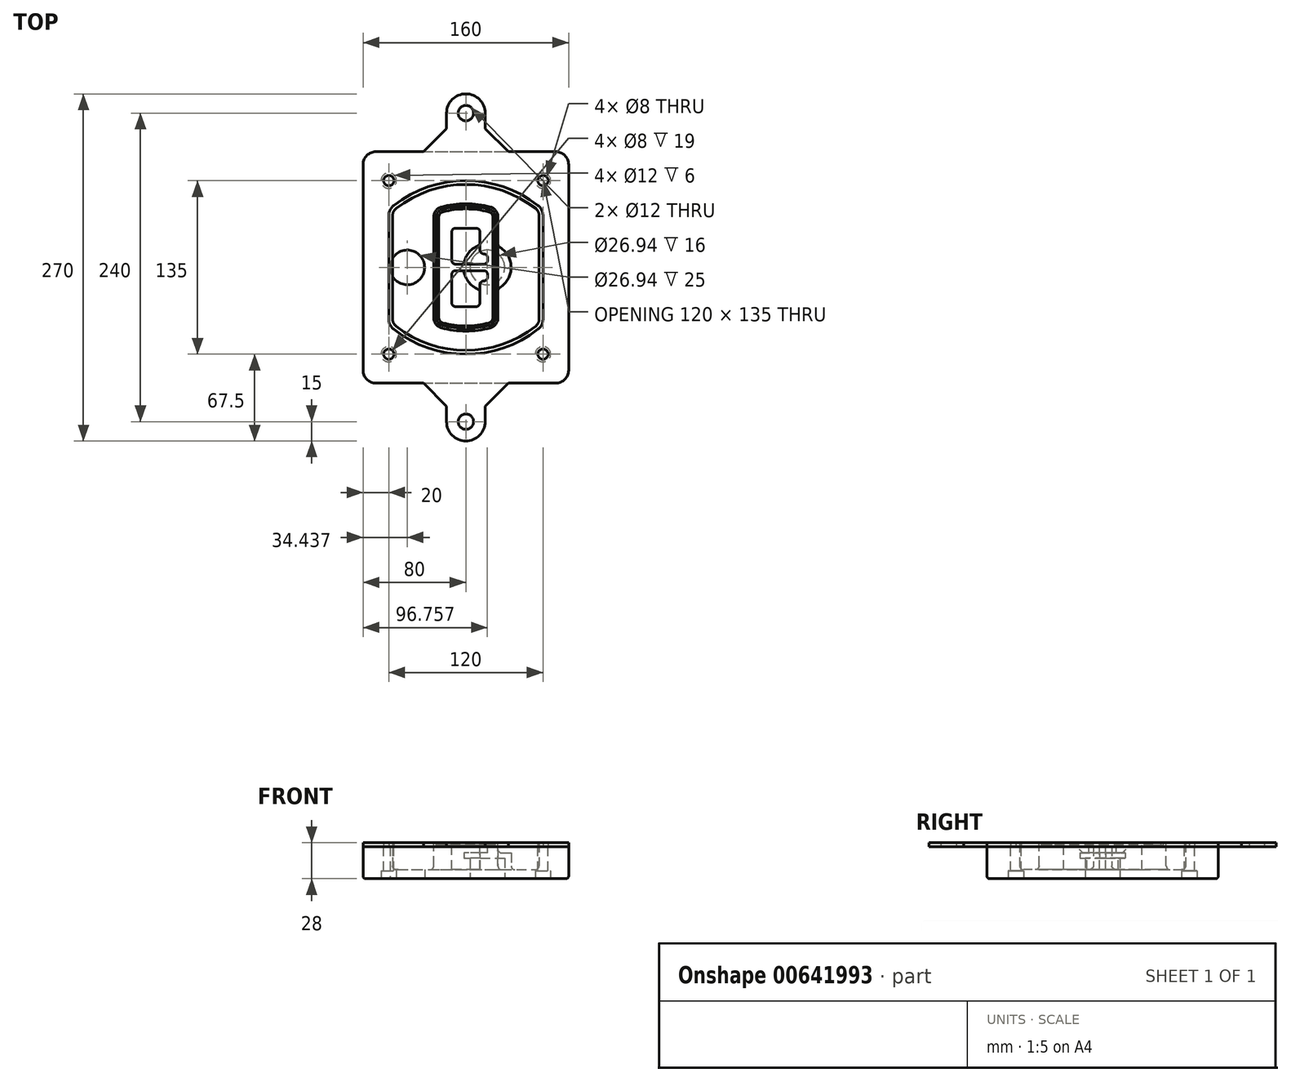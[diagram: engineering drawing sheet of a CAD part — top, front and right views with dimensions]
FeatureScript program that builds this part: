
annotation { "Feature Type Name" : "Feature", "Feature Type Description" : "" }
export const myFeature = defineFeature(function(context is Context, id is Id, definition is map)
    precondition{}
    {
        {
            var Q0;
            Q0=qCreatedBy(makeId("Top.planeOp"),FACE);
            var sketch = newSketch(context, id + "F0", { "sketchPlane" : qUnion([Q0])});
            skPoint(sketch, "E0.rect.middle", {"position": v(0, 0) * mm});
            skLineSegment(sketch, "E1.bottom", {"start": v(-70, -90) * mm, "end": v(70, -90) * mm});
            skLineSegment(sketch, "E1.top", {"start": v(-70, 90) * mm, "end": v(70, 90) * mm});
            skLineSegment(sketch, "E1.left", {"start": v(-80, -80) * mm, "end": v(-80, 80) * mm});
            skLineSegment(sketch, "E1.right", {"start": v(80, -80) * mm, "end": v(80, 80) * mm});
            skLineSegment(sketch, "E2", {"start": v(-80, 90) * mm, "end": v(80, -90) * mm, "construction": true});
            skLineSegment(sketch, "E3", {"start": v(80, 90) * mm, "end": v(-80, -90) * mm, "construction": true});
            skCircle(sketch, "E4", {"center": v(-60, 67.5) * mm, "radius": 4 * mm});
            skCircle(sketch, "E5", {"center": v(60, 67.5) * mm, "radius": 4 * mm});
            skCircle(sketch, "E6", {"center": v(60, -67.5) * mm, "radius": 4 * mm});
            skCircle(sketch, "E7", {"center": v(-60, -67.5) * mm, "radius": 4 * mm});
            skLineSegment(sketch, "E8", {"start": v(-60, 67.5) * mm, "end": v(60, 67.5) * mm, "construction": true});
            skLineSegment(sketch, "E9", {"start": v(60, 67.5) * mm, "end": v(60, -67.5) * mm, "construction": true});
            skLineSegment(sketch, "E10", {"start": v(60, -67.5) * mm, "end": v(-60, -67.5) * mm, "construction": true});
            skLineSegment(sketch, "E11", {"start": v(-60, -67.5) * mm, "end": v(-60, 67.5) * mm, "construction": true});
            skLineSegment(sketch, "E12", {"start": v(-60, 40.3) * mm, "end": v(-60, -40.3) * mm});
            skLineSegment(sketch, "E13", {"start": v(60, 40.3) * mm, "end": v(60, -40.3) * mm});
            skArc(sketch, "E14", {"start": v(56.15, 48.18) * mm, "mid": v(0, 67.5) * mm, "end": v(-56.15, 48.18) * mm});
            skArc(sketch, "E15", {"start": v(-56.15, -48.18) * mm, "mid": v(0, -67.5) * mm, "end": v(56.15, -48.18) * mm});
            skLineSegment(sketch, "E16", {"start": v(-60, 0) * mm, "end": v(60, 0) * mm, "construction": true});
            skPoint(sketch, "E17.visualSharp", {"position": v(-60, -45) * mm});
            skArc(sketch, "E17.filletArc", {"start": v(-60, -40.3) * mm, "mid": v(-58.99, -44.68) * mm, "end": v(-56.15, -48.18) * mm});
            skPoint(sketch, "E18.visualSharp", {"position": v(-60, 45) * mm});
            skArc(sketch, "E18.filletArc", {"start": v(-56.15, 48.18) * mm, "mid": v(-58.99, 44.68) * mm, "end": v(-60, 40.3) * mm});
            skPoint(sketch, "E19.visualSharp", {"position": v(60, 45) * mm});
            skArc(sketch, "E19.filletArc", {"start": v(60, 40.3) * mm, "mid": v(58.99, 44.68) * mm, "end": v(56.15, 48.18) * mm});
            skPoint(sketch, "E20.visualSharp", {"position": v(60, -45) * mm});
            skArc(sketch, "E20.filletArc", {"start": v(56.15, -48.18) * mm, "mid": v(58.99, -44.68) * mm, "end": v(60, -40.3) * mm});
            skPoint(sketch, "E21.visualSharp", {"position": v(-80, 90) * mm});
            skArc(sketch, "E21.filletArc", {"start": v(-70, 90) * mm, "mid": v(-77.07, 87.07) * mm, "end": v(-80, 80) * mm});
            skPoint(sketch, "E22.visualSharp", {"position": v(80, 90) * mm});
            skArc(sketch, "E22.filletArc", {"start": v(80, 80) * mm, "mid": v(77.07, 87.07) * mm, "end": v(70, 90) * mm});
            skPoint(sketch, "E23.visualSharp", {"position": v(80, -90) * mm});
            skArc(sketch, "E23.filletArc", {"start": v(70, -90) * mm, "mid": v(77.07, -87.07) * mm, "end": v(80, -80) * mm});
            skPoint(sketch, "E24.visualSharp", {"position": v(-80, -90) * mm});
            skArc(sketch, "E24.filletArc", {"start": v(-80, -80) * mm, "mid": v(-77.07, -87.07) * mm, "end": v(-70, -90) * mm});
            skArc(sketch, "E25.0", {"start": v(57, 40.3) * mm, "mid": v(56.3, 43.36) * mm, "end": v(54.3, 45.81) * mm});
            skLineSegment(sketch, "E25.1", {"start": v(57, 40.3) * mm, "end": v(57, -40.3) * mm});
            skArc(sketch, "E25.2", {"start": v(54.3, -45.81) * mm, "mid": v(56.3, -43.36) * mm, "end": v(57, -40.3) * mm});
            skArc(sketch, "E25.3", {"start": v(-54.3, -45.81) * mm, "mid": v(0, -64.5) * mm, "end": v(54.3, -45.81) * mm});
            skArc(sketch, "E25.4", {"start": v(-57, -40.3) * mm, "mid": v(-56.3, -43.36) * mm, "end": v(-54.3, -45.81) * mm});
            skArc(sketch, "E25.5", {"start": v(54.3, 45.81) * mm, "mid": v(0, 64.5) * mm, "end": v(-54.3, 45.81) * mm});
            skLineSegment(sketch, "E25.6", {"start": v(-57, 40.3) * mm, "end": v(-57, -40.3) * mm});
            skArc(sketch, "E25.7", {"start": v(-54.3, 45.81) * mm, "mid": v(-56.3, 43.36) * mm, "end": v(-57, 40.3) * mm});
            skArc(sketch, "E26.0", {"start": v(-58.62, 51.33) * mm, "mid": v(-62.58, 46.43) * mm, "end": v(-64, 40.3) * mm});
            skArc(sketch, "E26.1", {"start": v(58.62, 51.33) * mm, "mid": v(0, 71.5) * mm, "end": v(-58.62, 51.33) * mm});
            skArc(sketch, "E26.2", {"start": v(64, 40.3) * mm, "mid": v(62.58, 46.43) * mm, "end": v(58.62, 51.33) * mm});
            skLineSegment(sketch, "E26.3", {"start": v(64, 40.3) * mm, "end": v(64, -40.3) * mm});
            skArc(sketch, "E26.4", {"start": v(58.62, -51.33) * mm, "mid": v(62.58, -46.43) * mm, "end": v(64, -40.3) * mm});
            skLineSegment(sketch, "E26.5", {"start": v(-64, 40.3) * mm, "end": v(-64, -40.3) * mm});
            skArc(sketch, "E26.6", {"start": v(-58.62, -51.33) * mm, "mid": v(0, -71.5) * mm, "end": v(58.62, -51.33) * mm});
            skArc(sketch, "E26.7", {"start": v(-64, -40.3) * mm, "mid": v(-62.58, -46.43) * mm, "end": v(-58.62, -51.33) * mm});
            skSolve(sketch);
        }
        {
            var Q0;
            Q0=makeQuery(id+"F0.imprint","IMPRINT",FACE,{"disambiguationData":[TD([[makeQuery(id+"F0.imprint","IMPRINT",EDGE,{"derivedFrom":sQuery(id+"F0.wireOp",EDGE,"E1.bottom")}),1.0]])]});
            var Q1;
            Q1=makeQuery(id+"F0.imprint","IMPRINT",FACE,{"disambiguationData":[TD([[makeQuery(id+"F0.imprint","IMPRINT",EDGE,{"derivedFrom":sQuery(id+"F0.wireOp",EDGE,"E12")}),1.0]])]});
            var Q2;
            Q2=makeQuery(id+"F0.imprint","IMPRINT",FACE,{"disambiguationData":[TD([[makeQuery(id+"F0.imprint","IMPRINT",EDGE,{"derivedFrom":sQuery(id+"F0.wireOp",EDGE,"E25.0")}),1.0]])]});
            var Q3;
            Q3=makeQuery(id+"F0.imprint","IMPRINT",FACE,{"disambiguationData":[TD([[makeQuery(id+"F0.imprint","IMPRINT",EDGE,{"derivedFrom":sQuery(id+"F0.wireOp",EDGE,"E12")}),-1.0]])]});
            extrude(context, id + "F1", {"entities" : qUnion([Q0, Q1, Q2, Q3]), "oppositeDirection" : true, "depth" : 25 * mm});
        }
        {
            var Q0;
            Q0=makeQuery(id+"F0.imprint","IMPRINT",FACE,{"disambiguationData":[TD([[makeQuery(id+"F0.imprint","IMPRINT",EDGE,{"derivedFrom":sQuery(id+"F0.wireOp",EDGE,"E12")}),1.0]])]});
            extrude(context, id + "F2", {"entities" : qUnion([Q0]), "operationType" : NewBodyOperationType.ADD, "depth" : 3 * mm});
        }
        {
            var Q0;
            Q0=makeQuery(id+"F0.imprint","IMPRINT",FACE,{"disambiguationData":[TD([[makeQuery(id+"F0.imprint","IMPRINT",EDGE,{"derivedFrom":sQuery(id+"F0.wireOp",EDGE,"E25.0")}),1.0]])]});
            extrude(context, id + "F3", {"entities" : qUnion([Q0]), "operationType" : NewBodyOperationType.REMOVE, "oppositeDirection" : true, "depth" : 18 * mm});
        }
        {
            var Q0;
            Q0=makeQuery(id+"F2.opExtrude","CAP_FACE",FACE,{"disambiguationData":[OSD([sQuery(id+"F0.wireOp",EDGE,"E12"),sQuery(id+"F0.wireOp",EDGE,"E13"),sQuery(id+"F0.wireOp",EDGE,"E14"),sQuery(id+"F0.wireOp",EDGE,"E15"),sQuery(id+"F0.wireOp",EDGE,"E17.filletArc"),sQuery(id+"F0.wireOp",EDGE,"E18.filletArc"),sQuery(id+"F0.wireOp",EDGE,"E19.filletArc"),sQuery(id+"F0.wireOp",EDGE,"E20.filletArc"),sQuery(id+"F0.wireOp",EDGE,"E25.0"),sQuery(id+"F0.wireOp",EDGE,"E25.1"),sQuery(id+"F0.wireOp",EDGE,"E25.2"),sQuery(id+"F0.wireOp",EDGE,"E25.3"),sQuery(id+"F0.wireOp",EDGE,"E25.4"),sQuery(id+"F0.wireOp",EDGE,"E25.5"),sQuery(id+"F0.wireOp",EDGE,"E25.6"),sQuery(id+"F0.wireOp",EDGE,"E25.7")])],"isStart":false});
            var sketch = newSketch(context, id + "F4", { "sketchPlane" : qUnion([Q0])});
            skArc(sketch, "E27.0", {"start": v(-19.08, -46.97) * mm, "mid": v(0, -49.5) * mm, "end": v(19.08, -46.97) * mm});
            skArc(sketch, "E28.0", {"start": v(19.08, 46.97) * mm, "mid": v(0, 49.5) * mm, "end": v(-19.08, 46.97) * mm});
            skLineSegment(sketch, "E29", {"start": v(-25, 39.25) * mm, "end": v(-25, -39.25) * mm});
            skLineSegment(sketch, "E30", {"start": v(25, 39.25) * mm, "end": v(25, -39.25) * mm});
            skLineSegment(sketch, "E31", {"start": v(-25, 45.1) * mm, "end": v(25, 45.1) * mm, "construction": true});
            skLineSegment(sketch, "E32", {"start": v(-25, -45.1) * mm, "end": v(25, -45.1) * mm, "construction": true});
            skPoint(sketch, "E33.visualSharp", {"position": v(-25, 45.1) * mm});
            skArc(sketch, "E33.filletArc", {"start": v(-19.08, 46.97) * mm, "mid": v(-23.35, 44.11) * mm, "end": v(-25, 39.25) * mm});
            skPoint(sketch, "E34.visualSharp", {"position": v(25, 45.1) * mm});
            skArc(sketch, "E34.filletArc", {"start": v(25, 39.25) * mm, "mid": v(23.35, 44.11) * mm, "end": v(19.08, 46.97) * mm});
            skPoint(sketch, "E35.visualSharp", {"position": v(25, -45.1) * mm});
            skArc(sketch, "E35.filletArc", {"start": v(19.08, -46.97) * mm, "mid": v(23.35, -44.11) * mm, "end": v(25, -39.25) * mm});
            skPoint(sketch, "E36.visualSharp", {"position": v(-25, -45.1) * mm});
            skArc(sketch, "E36.filletArc", {"start": v(-25, -39.25) * mm, "mid": v(-23.35, -44.11) * mm, "end": v(-19.08, -46.97) * mm});
            skArc(sketch, "E37.0", {"start": v(54.3, 45.81) * mm, "mid": v(0, 64.5) * mm, "end": v(-54.3, 45.81) * mm});
            skArc(sketch, "E37.1", {"start": v(-54.3, 45.81) * mm, "mid": v(-56.3, 43.36) * mm, "end": v(-57, 40.3) * mm});
            skLineSegment(sketch, "E37.2", {"start": v(-57, 40.3) * mm, "end": v(-57, -40.3) * mm});
            skArc(sketch, "E37.3", {"start": v(-57, -40.3) * mm, "mid": v(-56.3, -43.36) * mm, "end": v(-54.3, -45.81) * mm});
            skArc(sketch, "E37.4", {"start": v(-54.3, -45.81) * mm, "mid": v(0, -64.5) * mm, "end": v(54.3, -45.81) * mm});
            skArc(sketch, "E37.5", {"start": v(54.3, -45.81) * mm, "mid": v(56.3, -43.36) * mm, "end": v(57, -40.3) * mm});
            skLineSegment(sketch, "E37.6", {"start": v(57, 40.3) * mm, "end": v(57, -40.3) * mm});
            skArc(sketch, "E37.7", {"start": v(57, 40.3) * mm, "mid": v(56.3, 43.36) * mm, "end": v(54.3, 45.81) * mm});
            skLineSegment(sketch, "E38.0", {"start": v(23, 39.25) * mm, "end": v(23, -39.25) * mm});
            skArc(sketch, "E38.1", {"start": v(18.56, -45.04) * mm, "mid": v(21.76, -42.9) * mm, "end": v(23, -39.25) * mm});
            skArc(sketch, "E38.2", {"start": v(-18.56, -45.04) * mm, "mid": v(0, -47.5) * mm, "end": v(18.56, -45.04) * mm});
            skArc(sketch, "E38.3", {"start": v(-23, -39.25) * mm, "mid": v(-21.76, -42.9) * mm, "end": v(-18.56, -45.04) * mm});
            skLineSegment(sketch, "E38.4", {"start": v(-23, 39.25) * mm, "end": v(-23, -39.25) * mm});
            skArc(sketch, "E38.5", {"start": v(23, 39.25) * mm, "mid": v(21.76, 42.9) * mm, "end": v(18.56, 45.04) * mm});
            skArc(sketch, "E38.6", {"start": v(-18.56, 45.04) * mm, "mid": v(-21.76, 42.9) * mm, "end": v(-23, 39.25) * mm});
            skArc(sketch, "E38.7", {"start": v(18.56, 45.04) * mm, "mid": v(0, 47.5) * mm, "end": v(-18.56, 45.04) * mm});
            skArc(sketch, "E39.0", {"start": v(21, 39.25) * mm, "mid": v(20.18, 41.68) * mm, "end": v(18.04, 43.1) * mm});
            skLineSegment(sketch, "E39.1", {"start": v(21, 39.25) * mm, "end": v(21, -39.25) * mm});
            skArc(sketch, "E39.2", {"start": v(18.04, -43.1) * mm, "mid": v(20.18, -41.68) * mm, "end": v(21, -39.25) * mm});
            skArc(sketch, "E39.3", {"start": v(-18.04, -43.1) * mm, "mid": v(0, -45.5) * mm, "end": v(18.04, -43.1) * mm});
            skArc(sketch, "E39.4", {"start": v(-21, -39.25) * mm, "mid": v(-20.18, -41.68) * mm, "end": v(-18.04, -43.1) * mm});
            skArc(sketch, "E39.5", {"start": v(18.04, 43.1) * mm, "mid": v(0, 45.5) * mm, "end": v(-18.04, 43.1) * mm});
            skLineSegment(sketch, "E39.6", {"start": v(-21, 39.25) * mm, "end": v(-21, -39.25) * mm});
            skArc(sketch, "E39.7", {"start": v(-18.04, 43.1) * mm, "mid": v(-20.18, 41.68) * mm, "end": v(-21, 39.25) * mm});
            skLineSegment(sketch, "E40", {"start": v(-25, 0) * mm, "end": v(25, 0) * mm, "construction": true});
            skLineSegment(sketch, "E41", {"start": v(-11, 5.5) * mm, "end": v(-11, 27.5) * mm});
            skLineSegment(sketch, "E42", {"start": v(-8, 30.5) * mm, "end": v(8, 30.5) * mm});
            skLineSegment(sketch, "E43", {"start": v(11, 27.5) * mm, "end": v(11, 13.5) * mm});
            skLineSegment(sketch, "E44", {"start": v(14, 10.5) * mm, "end": v(14, 10.5) * mm});
            skLineSegment(sketch, "E45", {"start": v(17, 7.5) * mm, "end": v(17, 5.5) * mm});
            skLineSegment(sketch, "E46", {"start": v(14, 2.5) * mm, "end": v(-8, 2.5) * mm});
            skPoint(sketch, "E47.visualSharp", {"position": v(-11, 30.5) * mm});
            skArc(sketch, "E47.filletArc", {"start": v(-8, 30.5) * mm, "mid": v(-10.12, 29.62) * mm, "end": v(-11, 27.5) * mm});
            skPoint(sketch, "E48.visualSharp", {"position": v(11, 30.5) * mm});
            skArc(sketch, "E48.filletArc", {"start": v(11, 27.5) * mm, "mid": v(10.12, 29.62) * mm, "end": v(8, 30.5) * mm});
            skPoint(sketch, "E49.visualSharp", {"position": v(11, 10.5) * mm});
            skArc(sketch, "E49.filletArc", {"start": v(11, 13.5) * mm, "mid": v(11.88, 11.38) * mm, "end": v(14, 10.5) * mm});
            skPoint(sketch, "E50.visualSharp", {"position": v(17, 10.5) * mm});
            skArc(sketch, "E50.filletArc", {"start": v(17, 7.5) * mm, "mid": v(16.12, 9.62) * mm, "end": v(14, 10.5) * mm});
            skPoint(sketch, "E51.visualSharp", {"position": v(17, 2.5) * mm});
            skArc(sketch, "E51.filletArc", {"start": v(14, 2.5) * mm, "mid": v(16.12, 3.38) * mm, "end": v(17, 5.5) * mm});
            skPoint(sketch, "E52.visualSharp", {"position": v(-11, 2.5) * mm});
            skArc(sketch, "E52.filletArc", {"start": v(-11, 5.5) * mm, "mid": v(-10.12, 3.38) * mm, "end": v(-8, 2.5) * mm});
            skLineSegment(sketch, "E53.0.MirrorCS", {"start": v(14, -2.5) * mm, "end": v(-8, -2.5) * mm});
            skArc(sketch, "E54.0.MirrorCS", {"start": v(-11, -5.5) * mm, "mid": v(-10.12, -3.38) * mm, "end": v(-8, -2.5) * mm});
            skLineSegment(sketch, "E55.0.MirrorCS", {"start": v(-11, -5.5) * mm, "end": v(-11, -27.5) * mm});
            skArc(sketch, "E56.0.MirrorCS", {"start": v(-8, -30.5) * mm, "mid": v(-10.12, -29.62) * mm, "end": v(-11, -27.5) * mm});
            skLineSegment(sketch, "E57.0.MirrorCS", {"start": v(-8, -30.5) * mm, "end": v(8, -30.5) * mm});
            skArc(sketch, "E58.0.MirrorCS", {"start": v(11, -27.5) * mm, "mid": v(10.12, -29.62) * mm, "end": v(8, -30.5) * mm});
            skLineSegment(sketch, "E59.0.MirrorCS", {"start": v(11, -27.5) * mm, "end": v(11, -13.5) * mm});
            skArc(sketch, "E60.0.MirrorCS", {"start": v(11, -13.5) * mm, "mid": v(11.88, -11.38) * mm, "end": v(14, -10.5) * mm});
            skArc(sketch, "E61.0.MirrorCS", {"start": v(17, -7.5) * mm, "mid": v(16.12, -9.62) * mm, "end": v(14, -10.5) * mm});
            skLineSegment(sketch, "E62.0.MirrorCS", {"start": v(17, -7.5) * mm, "end": v(17, -5.5) * mm});
            skArc(sketch, "E63.0.MirrorCS", {"start": v(14, -2.5) * mm, "mid": v(16.12, -3.38) * mm, "end": v(17, -5.5) * mm});
            skSolve(sketch);
        }
        {
            var Q0;
            Q0=makeQuery(id+"F4.imprint","IMPRINT",FACE,{"disambiguationData":[TD([[makeQuery(id+"F4.imprint","IMPRINT",EDGE,{"derivedFrom":sQuery(id+"F4.wireOp",EDGE,"E27.0")}),1.0]])]});
            var Q1;
            Q1=makeQuery(id+"F4.imprint","IMPRINT",FACE,{"disambiguationData":[TD([[makeQuery(id+"F4.imprint","IMPRINT",EDGE,{"derivedFrom":sQuery(id+"F4.wireOp",EDGE,"E38.0")}),-1.0]])]});
            var Q2;
            Q2=makeQuery(id+"F4.imprint","IMPRINT",FACE,{"disambiguationData":[TD([[makeQuery(id+"F4.imprint","IMPRINT",EDGE,{"derivedFrom":sQuery(id+"F4.wireOp",EDGE,"E39.0")}),1.0]])]});
            extrude(context, id + "F5", {"entities" : qUnion([Q0, Q1, Q2]), "operationType" : NewBodyOperationType.ADD, "endBound" : BoundingType.UP_TO_NEXT, "oppositeDirection" : true, "depth" : 25 * mm});
        }
        {
            var Q0;
            Q0=makeQuery(id+"F4.imprint","IMPRINT",FACE,{"disambiguationData":[TD([[makeQuery(id+"F4.imprint","IMPRINT",EDGE,{"derivedFrom":sQuery(id+"F4.wireOp",EDGE,"E38.0")}),-1.0]])]});
            extrude(context, id + "F6", {"entities" : qUnion([Q0]), "operationType" : NewBodyOperationType.REMOVE, "oppositeDirection" : true, "depth" : 2 * mm});
        }
        {
            var Q0;
            Q0=makeQuery(id+"F1.opExtrude","CAP_FACE",FACE,{"disambiguationData":[OSD([sQuery(id+"F0.wireOp",EDGE,"E1.bottom"),sQuery(id+"F0.wireOp",EDGE,"E1.top"),sQuery(id+"F0.wireOp",EDGE,"E1.left"),sQuery(id+"F0.wireOp",EDGE,"E1.right"),sQuery(id+"F0.wireOp",EDGE,"E4"),sQuery(id+"F0.wireOp",EDGE,"E5"),sQuery(id+"F0.wireOp",EDGE,"E6"),sQuery(id+"F0.wireOp",EDGE,"E7"),sQuery(id+"F0.wireOp",EDGE,"E21.filletArc"),sQuery(id+"F0.wireOp",EDGE,"E22.filletArc"),sQuery(id+"F0.wireOp",EDGE,"E23.filletArc"),sQuery(id+"F0.wireOp",EDGE,"E24.filletArc")])],"isStart":false});
            var sketch = newSketch(context, id + "F7", { "sketchPlane" : qUnion([Q0])});
            skCircle(sketch, "E64", {"center": v(16.76, 0) * mm, "radius": 13.47 * mm});
            skCircle(sketch, "E65", {"center": v(-45.56, 0) * mm, "radius": 13.47 * mm});
            skLineSegment(sketch, "E66", {"start": v(80, 0) * mm, "end": v(-80, 0) * mm});
            skCircle(sketch, "E67", {"center": v(16.76, 0) * mm, "radius": 18.47 * mm});
            skCircle(sketch, "E68", {"center": v(60, -67.5) * mm, "radius": 6 * mm});
            skCircle(sketch, "E69", {"center": v(-60, -67.5) * mm, "radius": 6 * mm});
            skCircle(sketch, "E70", {"center": v(-60, 67.5) * mm, "radius": 6 * mm});
            skCircle(sketch, "E71", {"center": v(60, 67.5) * mm, "radius": 6 * mm});
            skSolve(sketch);
        }
        {
            var Q0;
            {var subQ1=sQuery(id+"F7.wireOp",EDGE,"E66");var subQ4=sQuery(id+"F7.wireOp",EDGE,"E64");var subQ6=makeQuery(id+"F7.imprint","INTERSECT",VERTEX,{"disambiguationData":[OD(0.0)],"derivedFrom":[subQ4,subQ1]});Q0=makeQuery(id+"F7.imprint","IMPRINT",FACE,{"disambiguationData":[TD([[makeQuery(id+"F7.imprint","IMPRINT",EDGE,{"disambiguationData":[TD([[subQ6,-1.0]])],"derivedFrom":subQ4}),-1.0]])]});}
            var Q1;
            {var subQ0=sQuery(id+"F7.wireOp",EDGE,"E66");var subQ1=sQuery(id+"F7.wireOp",EDGE,"E64");var subQ3=makeQuery(id+"F7.imprint","INTERSECT",VERTEX,{"disambiguationData":[OD(0.0)],"derivedFrom":[subQ1,subQ0]});Q1=makeQuery(id+"F7.imprint","IMPRINT",FACE,{"disambiguationData":[TD([[makeQuery(id+"F7.imprint","IMPRINT",EDGE,{"disambiguationData":[TD([[subQ3,-1.0]])],"derivedFrom":subQ1}),1.0]])]});}
            var Q2;
            {var subQ0=sQuery(id+"F7.wireOp",EDGE,"E66");var subQ1=sQuery(id+"F7.wireOp",EDGE,"E64");var subQ3=makeQuery(id+"F7.imprint","INTERSECT",VERTEX,{"disambiguationData":[OD(0.0)],"derivedFrom":[subQ1,subQ0]});Q2=makeQuery(id+"F7.imprint","IMPRINT",FACE,{"disambiguationData":[TD([[makeQuery(id+"F7.imprint","IMPRINT",EDGE,{"disambiguationData":[TD([[subQ3,1.0]])],"derivedFrom":subQ1}),1.0]])]});}
            var Q3;
            {var subQ1=sQuery(id+"F7.wireOp",EDGE,"E66");var subQ4=sQuery(id+"F7.wireOp",EDGE,"E64");var subQ6=makeQuery(id+"F7.imprint","INTERSECT",VERTEX,{"disambiguationData":[OD(0.0)],"derivedFrom":[subQ4,subQ1]});Q3=makeQuery(id+"F7.imprint","IMPRINT",FACE,{"disambiguationData":[TD([[makeQuery(id+"F7.imprint","IMPRINT",EDGE,{"disambiguationData":[TD([[subQ6,1.0]])],"derivedFrom":subQ4}),-1.0]])]});}
            extrude(context, id + "F8", {"entities" : qUnion([Q0, Q1, Q2, Q3]), "operationType" : NewBodyOperationType.ADD, "oppositeDirection" : true, "depth" : 20 * mm});
        }
        {
            var Q0;
            {var subQ0=sQuery(id+"F7.wireOp",EDGE,"E66");var subQ1=sQuery(id+"F7.wireOp",EDGE,"E64");var subQ3=makeQuery(id+"F7.imprint","INTERSECT",VERTEX,{"disambiguationData":[OD(0.0)],"derivedFrom":[subQ1,subQ0]});Q0=makeQuery(id+"F7.imprint","IMPRINT",FACE,{"disambiguationData":[TD([[makeQuery(id+"F7.imprint","IMPRINT",EDGE,{"disambiguationData":[TD([[subQ3,-1.0]])],"derivedFrom":subQ1}),1.0]])]});}
            var Q1;
            {var subQ0=sQuery(id+"F7.wireOp",EDGE,"E66");var subQ1=sQuery(id+"F7.wireOp",EDGE,"E64");var subQ3=makeQuery(id+"F7.imprint","INTERSECT",VERTEX,{"disambiguationData":[OD(0.0)],"derivedFrom":[subQ1,subQ0]});Q1=makeQuery(id+"F7.imprint","IMPRINT",FACE,{"disambiguationData":[TD([[makeQuery(id+"F7.imprint","IMPRINT",EDGE,{"disambiguationData":[TD([[subQ3,1.0]])],"derivedFrom":subQ1}),1.0]])]});}
            extrude(context, id + "F9", {"entities" : qUnion([Q0, Q1]), "operationType" : NewBodyOperationType.REMOVE, "oppositeDirection" : true, "depth" : 16 * mm});
        }
        {
            var Q0;
            {var subQ0=sQuery(id+"F7.wireOp",EDGE,"E66");var subQ1=sQuery(id+"F7.wireOp",EDGE,"E65");var subQ3=makeQuery(id+"F7.imprint","INTERSECT",VERTEX,{"disambiguationData":[OD(0.0)],"derivedFrom":[subQ1,subQ0]});Q0=makeQuery(id+"F7.imprint","IMPRINT",FACE,{"disambiguationData":[TD([[makeQuery(id+"F7.imprint","IMPRINT",EDGE,{"disambiguationData":[TD([[subQ3,-1.0]])],"derivedFrom":subQ1}),1.0]])]});}
            var Q1;
            {var subQ0=sQuery(id+"F7.wireOp",EDGE,"E66");var subQ1=sQuery(id+"F7.wireOp",EDGE,"E65");var subQ3=makeQuery(id+"F7.imprint","INTERSECT",VERTEX,{"disambiguationData":[OD(0.0)],"derivedFrom":[subQ1,subQ0]});Q1=makeQuery(id+"F7.imprint","IMPRINT",FACE,{"disambiguationData":[TD([[makeQuery(id+"F7.imprint","IMPRINT",EDGE,{"disambiguationData":[TD([[subQ3,1.0]])],"derivedFrom":subQ1}),1.0]])]});}
            extrude(context, id + "F10", {"entities" : qUnion([Q0, Q1]), "operationType" : NewBodyOperationType.REMOVE, "oppositeDirection" : true, "depth" : 25 * mm});
        }
        {
            var Q0;
            Q0=makeQuery(id+"F7.imprint","IMPRINT",FACE,{"disambiguationData":[TD([[makeQuery(id+"F7.imprint","IMPRINT",EDGE,{"derivedFrom":sQuery(id+"F7.wireOp",EDGE,"E68")}),1.0]])]});
            var Q1;
            Q1=makeQuery(id+"F7.imprint","IMPRINT",FACE,{"disambiguationData":[TD([[makeQuery(id+"F7.imprint","IMPRINT",EDGE,{"derivedFrom":makeQuery(id+"F1.opExtrude","CAP_EDGE",EDGE,{"disambiguationData":[OSD([sQuery(id+"F0.wireOp",EDGE,"E5")])],"isStart":false})}),-1.0]])]});
            var Q2;
            Q2=makeQuery(id+"F7.imprint","IMPRINT",FACE,{"disambiguationData":[TD([[makeQuery(id+"F7.imprint","IMPRINT",EDGE,{"derivedFrom":sQuery(id+"F7.wireOp",EDGE,"E69")}),1.0]])]});
            var Q3;
            Q3=makeQuery(id+"F7.imprint","IMPRINT",FACE,{"disambiguationData":[TD([[makeQuery(id+"F7.imprint","IMPRINT",EDGE,{"derivedFrom":makeQuery(id+"F1.opExtrude","CAP_EDGE",EDGE,{"disambiguationData":[OSD([sQuery(id+"F0.wireOp",EDGE,"E4")])],"isStart":false})}),-1.0]])]});
            var Q4;
            Q4=makeQuery(id+"F7.imprint","IMPRINT",FACE,{"disambiguationData":[TD([[makeQuery(id+"F7.imprint","IMPRINT",EDGE,{"derivedFrom":sQuery(id+"F7.wireOp",EDGE,"E70")}),1.0]])]});
            var Q5;
            Q5=makeQuery(id+"F7.imprint","IMPRINT",FACE,{"disambiguationData":[TD([[makeQuery(id+"F7.imprint","IMPRINT",EDGE,{"derivedFrom":makeQuery(id+"F1.opExtrude","CAP_EDGE",EDGE,{"disambiguationData":[OSD([sQuery(id+"F0.wireOp",EDGE,"E7")])],"isStart":false})}),-1.0]])]});
            var Q6;
            Q6=makeQuery(id+"F7.imprint","IMPRINT",FACE,{"disambiguationData":[TD([[makeQuery(id+"F7.imprint","IMPRINT",EDGE,{"derivedFrom":sQuery(id+"F7.wireOp",EDGE,"E71")}),1.0]])]});
            var Q7;
            Q7=makeQuery(id+"F7.imprint","IMPRINT",FACE,{"disambiguationData":[TD([[makeQuery(id+"F7.imprint","IMPRINT",EDGE,{"derivedFrom":makeQuery(id+"F1.opExtrude","CAP_EDGE",EDGE,{"disambiguationData":[OSD([sQuery(id+"F0.wireOp",EDGE,"E6")])],"isStart":false})}),-1.0]])]});
            extrude(context, id + "F11", {"entities" : qUnion([Q0, Q1, Q2, Q3, Q4, Q5, Q6, Q7]), "operationType" : NewBodyOperationType.REMOVE, "oppositeDirection" : true, "depth" : 6 * mm});
        }
        {
            var Q0;
            Q0=makeQuery(id+"F9.boolean.opBoolean","COPY",FACE,{"derivedFrom":makeQuery(id+"F9.opExtrude","CAP_FACE",FACE,{"disambiguationData":[OSD([sQuery(id+"F7.wireOp",EDGE,"E64")])],"isStart":false})});
            var sketch = newSketch(context, id + "F12", { "sketchPlane" : qUnion([Q0])});
            skArc(sketch, "E72.0", {"start": v(11, 17.55) * mm, "mid": v(2.57, 11.82) * mm, "end": v(-1.54, 2.5) * mm});
            skArc(sketch, "E72.1", {"start": v(-1.54, -2.5) * mm, "mid": v(2.57, -11.82) * mm, "end": v(11, -17.55) * mm});
            skLineSegment(sketch, "E73", {"start": v(-1.54, -2.5) * mm, "end": v(14, -2.5) * mm});
            skLineSegment(sketch, "E74.0", {"start": v(14, 2.5) * mm, "end": v(-1.54, 2.5) * mm});
            skArc(sketch, "E74.1", {"start": v(14, 2.5) * mm, "mid": v(16.12, 3.38) * mm, "end": v(17, 5.5) * mm});
            skLineSegment(sketch, "E74.2", {"start": v(17, 7.5) * mm, "end": v(17, 5.5) * mm});
            skArc(sketch, "E74.3", {"start": v(17, 7.5) * mm, "mid": v(16.12, 9.62) * mm, "end": v(14, 10.5) * mm});
            skArc(sketch, "E74.4", {"start": v(11, 13.5) * mm, "mid": v(11.88, 11.38) * mm, "end": v(14, 10.5) * mm});
            skLineSegment(sketch, "E74.5", {"start": v(11, 17.55) * mm, "end": v(11, 13.5) * mm});
            skLineSegment(sketch, "E74.7", {"start": v(14, -2.5) * mm, "end": v(-1.54, -2.5) * mm});
            skArc(sketch, "E74.8", {"start": v(14, -2.5) * mm, "mid": v(16.12, -3.38) * mm, "end": v(17, -5.5) * mm});
            skLineSegment(sketch, "E74.9", {"start": v(17, -7.5) * mm, "end": v(17, -5.5) * mm});
            skArc(sketch, "E74.10", {"start": v(17, -7.5) * mm, "mid": v(16.12, -9.62) * mm, "end": v(14, -10.5) * mm});
            skArc(sketch, "E74.11", {"start": v(11, -13.5) * mm, "mid": v(11.88, -11.38) * mm, "end": v(14, -10.5) * mm});
            skLineSegment(sketch, "E74.12", {"start": v(11, -17.55) * mm, "end": v(11, -13.5) * mm});
            skPoint(sketch, "E75.orphan", {"position": v(11, -27.5) * mm});
            skPoint(sketch, "E76.orphan", {"position": v(-8, -2.5) * mm});
            skPoint(sketch, "E77.orphan", {"position": v(-8, 2.5) * mm});
            skPoint(sketch, "E78.orphan", {"position": v(11, 27.5) * mm});
            skSolve(sketch);
        }
        {
            var Q0;
            {var subQ7=sQuery(id+"F12.wireOp",EDGE,"E72.0");var subQ14=sQuery(id+"F12.wireOp",EDGE,"E72.1");var subQ16=sQuery(id+"F12.wireOp",EDGE,"E74.1");var subQ18=sQuery(id+"F12.wireOp",EDGE,"E74.8");Q0=qUnion([makeQuery(id+"F12.imprint","IMPRINT",FACE,{"disambiguationData":[TD([[makeQuery(id+"F12.imprint","IMPRINT",EDGE,{"derivedFrom":subQ7}),1.0]])]}),makeQuery(id+"F12.imprint","IMPRINT",FACE,{"disambiguationData":[TD([[makeQuery(id+"F12.imprint","IMPRINT",EDGE,{"derivedFrom":subQ14}),1.0]])]}),makeQuery(id+"F12.imprint","IMPRINT",FACE,{"disambiguationData":[TD([[makeQuery(id+"F12.imprint","IMPRINT",EDGE,{"derivedFrom":subQ16}),1.0]])]}),makeQuery(id+"F12.imprint","IMPRINT",FACE,{"disambiguationData":[TD([[makeQuery(id+"F12.imprint","IMPRINT",EDGE,{"derivedFrom":subQ18}),-1.0]])]})]);}
            var Q1;
            Q1=makeQuery(id+"F5.boolean.opBoolean","SPLIT",FACE,{"disambiguationData":[TD([makeQuery(id+"F5.opExtrude","SWEPT_FACE",FACE,{"disambiguationData":[OSD([sQuery(id+"F4.wireOp",EDGE,"E41")])]})])],"derivedFrom":makeQuery(id+"F3.boolean.opBoolean","COPY",FACE,{"derivedFrom":makeQuery(id+"F3.opExtrude","CAP_FACE",FACE,{"disambiguationData":[OSD([sQuery(id+"F0.wireOp",EDGE,"E25.0"),sQuery(id+"F0.wireOp",EDGE,"E25.1"),sQuery(id+"F0.wireOp",EDGE,"E25.2"),sQuery(id+"F0.wireOp",EDGE,"E25.3"),sQuery(id+"F0.wireOp",EDGE,"E25.4"),sQuery(id+"F0.wireOp",EDGE,"E25.5"),sQuery(id+"F0.wireOp",EDGE,"E25.6"),sQuery(id+"F0.wireOp",EDGE,"E25.7")])],"isStart":false})})});
            extrude(context, id + "F13", {"entities" : qUnion([Q0]), "operationType" : NewBodyOperationType.REMOVE, "endBound" : BoundingType.UP_TO_SURFACE, "endBoundEntityFace" : qUnion([Q1]), "depth" : 25 * mm});
        }
        {
            var Q0;
            Q0=makeQuery(id+"F3.boolean.opBoolean","COPY",EDGE,{"derivedFrom":makeQuery(id+"F3.opExtrude","CAP_EDGE",EDGE,{"disambiguationData":[OSD([sQuery(id+"F0.wireOp",EDGE,"E25.6")])],"isStart":false})});
            var Q1;
            Q1=makeQuery(id+"F8.boolean.opBoolean","INTERSECT",EDGE,{"derivedFrom":[makeQuery(id+"F5.opExtrude","SWEPT_FACE",FACE,{"disambiguationData":[OSD([sQuery(id+"F4.wireOp",EDGE,"E30")])]}),makeQuery(id+"F8.opExtrude","CAP_FACE",FACE,{"disambiguationData":[OSD([sQuery(id+"F7.wireOp",EDGE,"E67")])],"isStart":false})]});
            var Q2;
            Q2=makeQuery(id+"F8.boolean.opBoolean","INTERSECT",EDGE,{"disambiguationData":[OD(1.0)],"derivedFrom":[makeQuery(id+"F5.opExtrude","SWEPT_FACE",FACE,{"disambiguationData":[OSD([sQuery(id+"F4.wireOp",EDGE,"E30")])]}),makeQuery(id+"F8.opExtrude","SWEPT_FACE",FACE,{"disambiguationData":[OSD([sQuery(id+"F7.wireOp",EDGE,"E67")])]})]});
            var Q3;
            {var subQ0=sQuery(id+"F4.wireOp",EDGE,"E30");Q3=makeQuery(id+"F8.boolean.opBoolean","SPLIT",EDGE,{"disambiguationData":[TD([makeQuery(id+"F5.opExtrude","SWEPT_FACE",FACE,{"disambiguationData":[OSD([sQuery(id+"F4.wireOp",EDGE,"E35.filletArc")])]})])],"derivedFrom":makeQuery(id+"F5.opExtrude","CAP_EDGE",EDGE,{"disambiguationData":[OSD([subQ0])],"isStart":false})});}
            var Q4;
            {var subQ0=sQuery(id+"F0.wireOp",EDGE,"E25.7");var subQ1=sQuery(id+"F0.wireOp",EDGE,"E25.1");var subQ2=sQuery(id+"F0.wireOp",EDGE,"E25.6");var subQ3=sQuery(id+"F0.wireOp",EDGE,"E25.5");var subQ4=sQuery(id+"F0.wireOp",EDGE,"E25.4");var subQ5=sQuery(id+"F0.wireOp",EDGE,"E25.0");var subQ6=sQuery(id+"F0.wireOp",EDGE,"E25.2");var subQ7=sQuery(id+"F0.wireOp",EDGE,"E25.3");Q4=makeQuery(id+"F8.boolean.opBoolean","INTERSECT",EDGE,{"derivedFrom":[makeQuery(id+"F5.boolean.opBoolean","SPLIT",FACE,{"disambiguationData":[TD([makeQuery(id+"F2.opExtrude","SWEPT_FACE",FACE,{"disambiguationData":[OSD([subQ5])]})])],"derivedFrom":makeQuery(id+"F3.boolean.opBoolean","COPY",FACE,{"derivedFrom":makeQuery(id+"F3.opExtrude","CAP_FACE",FACE,{"disambiguationData":[OSD([subQ5,subQ1,subQ6,subQ7,subQ4,subQ3,subQ2,subQ0])],"isStart":false})})}),makeQuery(id+"F8.opExtrude","SWEPT_FACE",FACE,{"disambiguationData":[OSD([sQuery(id+"F7.wireOp",EDGE,"E67")])]})]});}
            var Q5;
            Q5=makeQuery(id+"F8.boolean.opBoolean","INTERSECT",EDGE,{"disambiguationData":[OD(0.0)],"derivedFrom":[makeQuery(id+"F5.opExtrude","SWEPT_FACE",FACE,{"disambiguationData":[OSD([sQuery(id+"F4.wireOp",EDGE,"E30")])]}),makeQuery(id+"F8.opExtrude","SWEPT_FACE",FACE,{"disambiguationData":[OSD([sQuery(id+"F7.wireOp",EDGE,"E67")])]})]});
            fillet(context, id + "F14", {"entities" : qUnion([Q0, Q1, Q2, Q3, Q4, Q5]), "radius" : 3 * mm, "tangentPropagation" : true, "allowEdgeOverflow" : false});
        }
        {
            var Q0;
            Q0=makeQuery(id+"F1.opExtrude","CAP_EDGE",EDGE,{"disambiguationData":[OSD([sQuery(id+"F0.wireOp",EDGE,"E1.bottom")])],"isStart":false});
            fillet(context, id + "F15", {"entities" : qUnion([Q0]), "radius" : 2 * mm, "tangentPropagation" : true, "allowEdgeOverflow" : false});
        }
        {
            var Q0;
            {var subQ0=sQuery(id+"F0.wireOp",EDGE,"E21.filletArc");var subQ1=sQuery(id+"F0.wireOp",EDGE,"E7");var subQ2=sQuery(id+"F0.wireOp",EDGE,"E6");var subQ3=sQuery(id+"F0.wireOp",EDGE,"E5");var subQ4=sQuery(id+"F0.wireOp",EDGE,"E4");var subQ5=sQuery(id+"F0.wireOp",EDGE,"E22.filletArc");var subQ6=sQuery(id+"F0.wireOp",EDGE,"E1.bottom");var subQ7=sQuery(id+"F0.wireOp",EDGE,"E1.right");var subQ8=sQuery(id+"F0.wireOp",EDGE,"E1.top");var subQ9=sQuery(id+"F0.wireOp",EDGE,"E1.left");var subQ10=sQuery(id+"F0.wireOp",EDGE,"E23.filletArc");var subQ11=sQuery(id+"F0.wireOp",EDGE,"E24.filletArc");Q0=makeQuery(id+"F2.boolean.opBoolean","SPLIT",FACE,{"disambiguationData":[TD([makeQuery(id+"F1.opExtrude","SWEPT_FACE",FACE,{"disambiguationData":[OSD([subQ6])]})])],"derivedFrom":makeQuery(id+"F1.opExtrude","CAP_FACE",FACE,{"disambiguationData":[OSD([subQ6,subQ8,subQ9,subQ7,subQ4,subQ3,subQ2,subQ1,subQ0,subQ5,subQ10,subQ11])],"isStart":true})});}
            var sketch = newSketch(context, id + "F16", { "sketchPlane" : qUnion([Q0])});
            skLineSegment(sketch, "E79", {"start": v(0, 90) * mm, "end": v(0, 120) * mm, "construction": true});
            skLineSegment(sketch, "E80", {"start": v(-33, 90) * mm, "end": v(-15, 108) * mm});
            skLineSegment(sketch, "E81", {"start": v(-15, 108) * mm, "end": v(-15, 120) * mm});
            skCircle(sketch, "E82", {"center": v(0, 120) * mm, "radius": 6 * mm});
            skLineSegment(sketch, "E83", {"start": v(33, 90) * mm, "end": v(15, 108) * mm});
            skLineSegment(sketch, "E84", {"start": v(15, 108) * mm, "end": v(15, 120) * mm});
            skArc(sketch, "E85", {"start": v(15, 120) * mm, "mid": v(0, 135) * mm, "end": v(-15, 120) * mm});
            skLineSegment(sketch, "E86", {"start": v(-80, 0) * mm, "end": v(80, 0) * mm, "construction": true});
            skLineSegment(sketch, "E87.MirrorCS", {"start": v(33, -90) * mm, "end": v(15, -108) * mm});
            skLineSegment(sketch, "E88.MirrorCS", {"start": v(15, -108) * mm, "end": v(15, -120) * mm});
            skArc(sketch, "E89.MirrorCS", {"start": v(15, -120) * mm, "mid": v(0, -135) * mm, "end": v(-15, -120) * mm});
            skCircle(sketch, "E90.MirrorC", {"center": v(0, -120) * mm, "radius": 6 * mm});
            skLineSegment(sketch, "E91.MirrorCS", {"start": v(0, -90) * mm, "end": v(0, -120) * mm, "construction": true});
            skLineSegment(sketch, "E92.MirrorCS", {"start": v(-15, -108) * mm, "end": v(-15, -120) * mm});
            skLineSegment(sketch, "E93.MirrorCS", {"start": v(-33, -90) * mm, "end": v(-15, -108) * mm});
            skSolve(sketch);
        }
        {
            var Q0;
            {var subQ1=sQuery(id+"F16.wireOp",EDGE,"E80");Q0=makeQuery(id+"F16.imprint","IMPRINT",FACE,{"disambiguationData":[TD([[makeQuery(id+"F16.imprint","IMPRINT",EDGE,{"derivedFrom":subQ1}),-1.0]])]});}
            var Q1;
            {var subQ0=sQuery(id+"F16.wireOp",EDGE,"E87.MirrorCS");Q1=makeQuery(id+"F16.imprint","IMPRINT",FACE,{"disambiguationData":[TD([[makeQuery(id+"F16.imprint","IMPRINT",EDGE,{"derivedFrom":subQ0}),-1.0]])]});}
            var Q2;
            Q2=makeQuery(id+"F16.imprint","IMPRINT",FACE,{"disambiguationData":[TD([[makeQuery(id+"F16.imprint","IMPRINT",EDGE,{"derivedFrom":makeQuery(id+"F1.opExtrude","CAP_EDGE",EDGE,{"disambiguationData":[OSD([sQuery(id+"F0.wireOp",EDGE,"E1.left")])],"isStart":true})}),-1.0]])]});
            var Q3;
            Q3=makeQuery(id+"F2.opExtrude","CAP_FACE",FACE,{"disambiguationData":[OSD([sQuery(id+"F0.wireOp",EDGE,"E12"),sQuery(id+"F0.wireOp",EDGE,"E13"),sQuery(id+"F0.wireOp",EDGE,"E14"),sQuery(id+"F0.wireOp",EDGE,"E15"),sQuery(id+"F0.wireOp",EDGE,"E17.filletArc"),sQuery(id+"F0.wireOp",EDGE,"E18.filletArc"),sQuery(id+"F0.wireOp",EDGE,"E19.filletArc"),sQuery(id+"F0.wireOp",EDGE,"E20.filletArc"),sQuery(id+"F0.wireOp",EDGE,"E25.0"),sQuery(id+"F0.wireOp",EDGE,"E25.1"),sQuery(id+"F0.wireOp",EDGE,"E25.2"),sQuery(id+"F0.wireOp",EDGE,"E25.3"),sQuery(id+"F0.wireOp",EDGE,"E25.4"),sQuery(id+"F0.wireOp",EDGE,"E25.5"),sQuery(id+"F0.wireOp",EDGE,"E25.6"),sQuery(id+"F0.wireOp",EDGE,"E25.7")])],"isStart":false});
            extrude(context, id + "F17", {"entities" : qUnion([Q0, Q1, Q2]), "endBound" : BoundingType.UP_TO_SURFACE, "depth" : 25 * mm, "endBoundEntityFace" : qUnion([Q3]), "offsetDistance" : 25 * mm});
        }
    });
